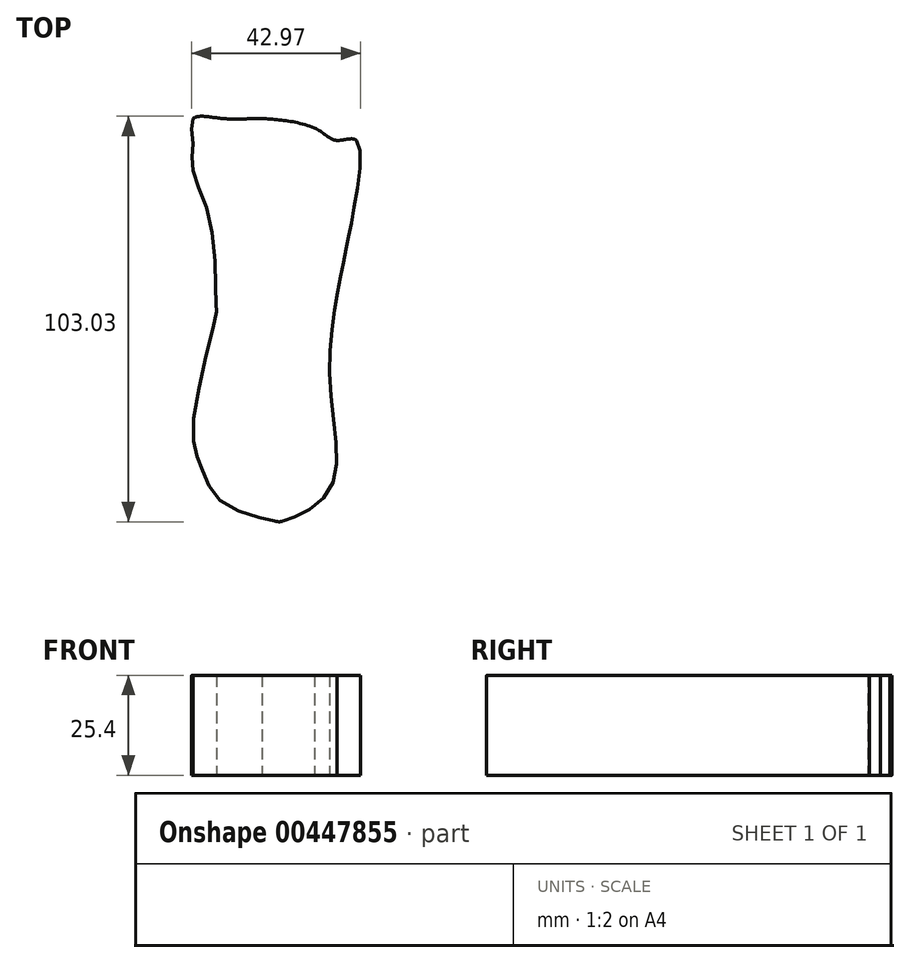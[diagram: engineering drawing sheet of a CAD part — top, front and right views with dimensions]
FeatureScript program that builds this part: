
annotation { "Feature Type Name" : "Feature", "Feature Type Description" : "" }
export const myFeature = defineFeature(function(context is Context, id is Id, definition is map)
    precondition{}
    {
        {
            var Q0;
            Q0=qCreatedBy(makeId("Top.planeOp"),FACE);
            var sketch = newSketch(context, id + "F0", { "sketchPlane" : qUnion([Q0])});
            skLineSegment(sketch, "E0.top", {"start": v(20.75, -46.2) * mm, "end": v(22.9, -46.2) * mm});
            skLineSegment(sketch, "E0.left", {"start": v(-0.24, 65.89) * mm, "end": v(-0.24, 65.89) * mm});
            skLineSegment(sketch, "E1", {"start": v(-0.24, 43.84) * mm, "end": v(-0.24, 43.84) * mm});
            skPoint(sketch, "E2", {"position": v(-0.24, 56.08) * mm});
            skPoint(sketch, "E3", {"position": v(0, 56.08) * mm});
            skPoint(sketch, "E4", {"position": v(-0.24, 65.89) * mm});
            skPoint(sketch, "E5", {"position": v(3.56, 75.7) * mm});
            skPoint(sketch, "E6", {"position": v(10.67, 75.7) * mm});
            skPoint(sketch, "E7", {"position": v(20.34, 72.85) * mm});
            skPoint(sketch, "E8", {"position": v(14.88, 74.07) * mm});
            skPoint(sketch, "E9", {"position": v(26.04, 70.42) * mm});
            skPoint(sketch, "E10", {"position": v(31.73, 68.07) * mm});
            skPoint(sketch, "E11", {"position": v(38.78, 61.75) * mm});
            skPoint(sketch, "E12", {"position": v(34.9, -13.5) * mm});
            skPoint(sketch, "E13", {"position": v(34.54, -38.57) * mm});
            skPoint(sketch, "E14", {"position": v(22.9, -46.2) * mm});
            skPoint(sketch, "E15", {"position": v(7.5, -41.47) * mm});
            skPoint(sketch, "E16", {"position": v(1.94, -32.27) * mm});
            skPoint(sketch, "E17", {"position": v(0, -22.02) * mm});
            skPoint(sketch, "E18", {"position": v(5.82, 6.42) * mm});
            skPoint(sketch, "E19", {"position": v(5.82, 8.72) * mm});
            skPoint(sketch, "E20", {"position": v(4.44, 29.45) * mm});
            skPoint(sketch, "E21", {"position": v(41.5, 50.54) * mm});
            skPoint(sketch, "E22", {"position": v(41.19, 35) * mm});
            skPoint(sketch, "E23", {"position": v(38.9, 23.15) * mm});
            skPoint(sketch, "E24", {"position": v(36.52, 11.01) * mm});
            skPoint(sketch, "E25", {"position": v(-0.24, 43.84) * mm});
            skPoint(sketch, "E26.21.internal.snap0", {"position": v(20.75, -46.2) * mm});
            skPoint(sketch, "E27.orphan", {"position": v(41.74, -46.2) * mm});
            skPoint(sketch, "E28.orphan", {"position": v(-0.24, -46.2) * mm});
            skPoint(sketch, "E29.orphan", {"position": v(-0.24, 75.7) * mm});
            skPoint(sketch, "E30", {"position": v(7.47, 56.08) * mm});
            skPoint(sketch, "E31", {"position": v(17.47, 56.08) * mm});
            skPoint(sketch, "E32", {"position": v(30.9, 53.7) * mm});
            skFitSpline(sketch, "E33", {"points": [v(7.47, 56.08) * mm, v(0, 56.08) * mm, v(-0.11, 59.77) * mm, v(-0.28, 62.81) * mm, v(-0.24, 65.89) * mm, v(1.26, 72.7) * mm, v(3.56, 75.7) * mm, v(10.67, 75.7) * mm, v(14.88, 74.07) * mm, v(20.34, 72.85) * mm, v(26.04, 70.42) * mm, v(31.73, 68.07) * mm, v(38.78, 61.75) * mm, v(41.5, 50.54) * mm, v(30.9, 53.7) * mm, v(17.47, 56.08) * mm, v(7.47, 56.08) * mm]});
            skFitSpline(sketch, "E34", {"points": [v(-0.24, 43.84) * mm, v(4.44, 29.45) * mm, v(5.82, 8.72) * mm, v(5.82, 6.42) * mm, v(0, -22.02) * mm, v(1.94, -32.27) * mm, v(7.5, -41.47) * mm, v(20.75, -46.2) * mm, v(22.9, -46.2) * mm, v(34.54, -38.57) * mm, v(34.9, -13.5) * mm, v(36.52, 11.01) * mm, v(38.9, 23.15) * mm, v(41.19, 35) * mm, v(41.5, 50.54) * mm, v(36.52, 50.54) * mm, v(30.9, 53.7) * mm, v(17.47, 56.08) * mm, v(7.47, 56.08) * mm, v(0, 56.08) * mm, v(0, 50.54) * mm, v(-0.24, 43.84) * mm]});
            skSolve(sketch);
        }
        {
            var Q0;
            {var subQ0=sQuery(id+"F0.wireOp",EDGE,"E0.top");Q0=makeQuery(id+"F0.imprint","IMPRINT",FACE,{"disambiguationData":[TD([[makeQuery(id+"F0.imprint","IMPRINT",EDGE,{"derivedFrom":subQ0}),-1.0]])]});}
            var Q1;
            {var subQ0=sQuery(id+"F0.wireOp",EDGE,"E34");var subQ1=sQuery(id+"F0.wireOp",EDGE,"E33");var subQ2=makeQuery(id+"F0.imprint","INTERSECT",VERTEX,{"disambiguationData":[OD(0.0)],"derivedFrom":[subQ1,subQ0]});Q1=makeQuery(id+"F0.imprint","IMPRINT",FACE,{"disambiguationData":[TD([[makeQuery(id+"F0.imprint","IMPRINT",EDGE,{"disambiguationData":[TD([[subQ2,1.0]])],"derivedFrom":subQ1}),-1.0]])]});}
            var Q2;
            {var subQ0=sQuery(id+"F0.wireOp",EDGE,"E34");var subQ1=sQuery(id+"F0.wireOp",EDGE,"E33");var subQ2=makeQuery(id+"F0.imprint","INTERSECT",VERTEX,{"disambiguationData":[OD(1.0)],"derivedFrom":[subQ1,subQ0]});Q2=makeQuery(id+"F0.imprint","IMPRINT",FACE,{"disambiguationData":[TD([[makeQuery(id+"F0.imprint","IMPRINT",EDGE,{"disambiguationData":[TD([[subQ2,-1.0]])],"derivedFrom":subQ1}),-1.0]])]});}
            var Q3;
            {var subQ4=sQuery(id+"F0.wireOp",EDGE,"E0.top");Q3=makeQuery(id+"F0.imprint","IMPRINT",FACE,{"disambiguationData":[TD([[makeQuery(id+"F0.imprint","IMPRINT",EDGE,{"derivedFrom":subQ4}),1.0]])]});}
            extrude(context, id + "F1", {"entities" : qUnion([Q0, Q1, Q2, Q3]), "depth" : 25.4 * mm});
        }
    });
